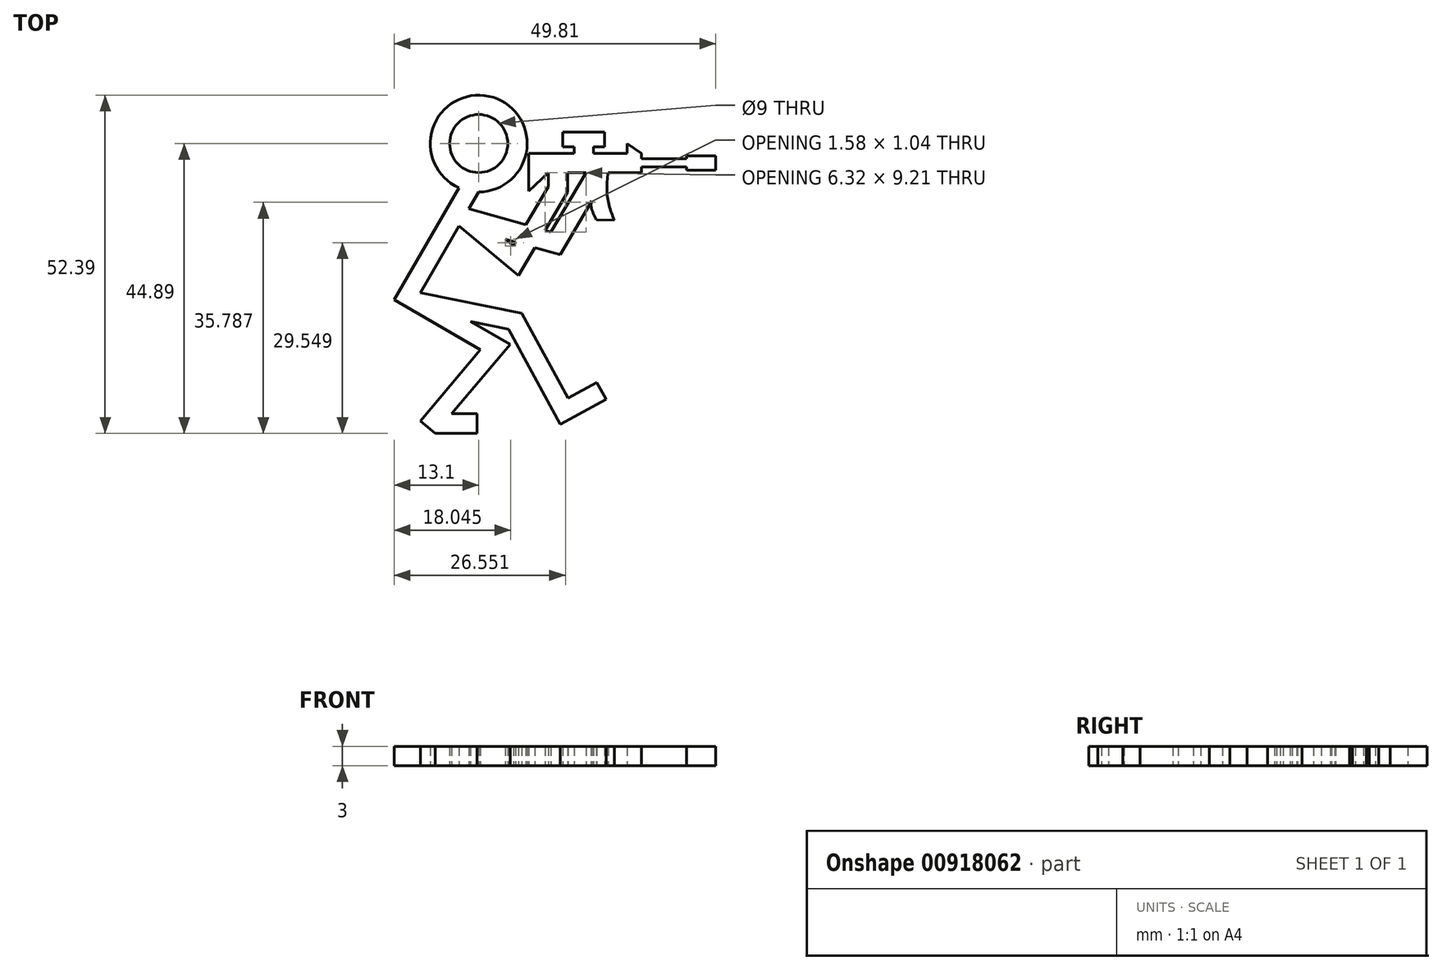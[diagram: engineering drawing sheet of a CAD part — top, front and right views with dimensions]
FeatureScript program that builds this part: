
annotation { "Feature Type Name" : "Feature", "Feature Type Description" : "" }
export const myFeature = defineFeature(function(context is Context, id is Id, definition is map)
    precondition{}
    {
        {
            var Q0;
            Q0=qCreatedBy(makeId("Top.planeOp"),FACE);
            var sketch = newSketch(context, id + "F0", { "sketchPlane" : qUnion([Q0])});
            skCircle(sketch, "E0", {"center": v(0, 0) * mm, "radius": 7.5 * mm});
            skCircle(sketch, "E1.0", {"center": v(0, 0) * mm, "radius": 4.5 * mm});
            skLineSegment(sketch, "E2", {"start": v(0, -7.5) * mm, "end": v(-10.5, -25.7) * mm});
            skLineSegment(sketch, "E3", {"start": v(-10.5, -25.7) * mm, "end": v(-13.1, -24.2) * mm});
            skLineSegment(sketch, "E4", {"start": v(-13.1, -24.2) * mm, "end": v(-3.08, -6.84) * mm});
            skLineSegment(sketch, "E5", {"start": v(0, -7.5) * mm, "end": v(0, -12.14) * mm, "construction": true});
            skLineSegment(sketch, "E6", {"start": v(-10.5, -25.7) * mm, "end": v(0.27, -31.9) * mm});
            skLineSegment(sketch, "E7", {"start": v(0.27, -31.9) * mm, "end": v(-9, -42.96) * mm});
            skLineSegment(sketch, "E8", {"start": v(-9, -42.96) * mm, "end": v(-6.7, -44.89) * mm});
            skLineSegment(sketch, "E9", {"start": v(-6.7, -44.89) * mm, "end": v(4.87, -31.1) * mm});
            skLineSegment(sketch, "E10", {"start": v(4.87, -31.1) * mm, "end": v(-9, -23.1) * mm});
            skLineSegment(sketch, "E11", {"start": v(-10.5, -25.7) * mm, "end": v(4.62, -28.75) * mm});
            skLineSegment(sketch, "E12", {"start": v(4.62, -28.75) * mm, "end": v(12.65, -43.5) * mm});
            skLineSegment(sketch, "E13", {"start": v(12.65, -43.5) * mm, "end": v(15.29, -42.07) * mm});
            skLineSegment(sketch, "E14", {"start": v(15.29, -42.07) * mm, "end": v(6.68, -26.26) * mm});
            skLineSegment(sketch, "E15", {"start": v(6.68, -26.26) * mm, "end": v(-9, -23.1) * mm});
            skLineSegment(sketch, "E16", {"start": v(-1.5, -10.1) * mm, "end": v(5.4, -15.86) * mm});
            skLineSegment(sketch, "E17", {"start": v(5.4, -15.86) * mm, "end": v(10.79, -6.68) * mm});
            skLineSegment(sketch, "E18", {"start": v(10.79, -6.68) * mm, "end": v(10.79, -4.5) * mm});
            skLineSegment(sketch, "E19", {"start": v(10.79, -4.5) * mm, "end": v(13.79, -4.5) * mm});
            skLineSegment(sketch, "E20", {"start": v(13.79, -4.5) * mm, "end": v(13.79, -7.5) * mm});
            skLineSegment(sketch, "E21", {"start": v(13.79, -7.5) * mm, "end": v(6.18, -20.43) * mm});
            skLineSegment(sketch, "E22", {"start": v(6.18, -20.43) * mm, "end": v(-3.02, -12.74) * mm});
            skLineSegment(sketch, "E23", {"start": v(4.15, -14.82) * mm, "end": v(12.61, -17.23) * mm});
            skLineSegment(sketch, "E24", {"start": v(12.61, -17.23) * mm, "end": v(20.1, -4.5) * mm});
            skLineSegment(sketch, "E25", {"start": v(20.1, -4.5) * mm, "end": v(16.61, -4.5) * mm});
            skLineSegment(sketch, "E26", {"start": v(16.61, -4.5) * mm, "end": v(11.2, -13.7) * mm});
            skLineSegment(sketch, "E27", {"start": v(11.2, -13.7) * mm, "end": v(-1.5, -10.1) * mm});
            skLineSegment(sketch, "E28.bottom", {"start": v(8.79, -4.5) * mm, "end": v(25.18, -4.5) * mm});
            skLineSegment(sketch, "E28.top", {"start": v(8.79, -1.5) * mm, "end": v(25.18, -1.5) * mm});
            skLineSegment(sketch, "E28.left", {"start": v(8.79, -4.5) * mm, "end": v(8.79, -1.5) * mm});
            skLineSegment(sketch, "E28.right", {"start": v(25.18, -4.5) * mm, "end": v(25.18, -1.5) * mm});
            skLineSegment(sketch, "E29.bottom", {"start": v(14.79, -1.5) * mm, "end": v(17.79, -1.5) * mm});
            skLineSegment(sketch, "E29.top", {"start": v(14.79, -0.5) * mm, "end": v(17.79, -0.5) * mm});
            skLineSegment(sketch, "E29.left", {"start": v(14.79, -1.5) * mm, "end": v(14.79, -0.5) * mm});
            skLineSegment(sketch, "E29.right", {"start": v(17.79, -1.5) * mm, "end": v(17.79, -0.5) * mm});
            skLineSegment(sketch, "E30", {"start": v(25.18, -1.5) * mm, "end": v(23, 0) * mm});
            skLineSegment(sketch, "E31", {"start": v(23, 0) * mm, "end": v(23, -1.5) * mm});
            skPoint(sketch, "E32.orphan", {"position": v(8.72, -16.12) * mm});
            skFitSpline(sketch, "E33", {"points": [v(20.1, -4.5) * mm, v(21.04, -11.87) * mm], "startDerivative": vector(-1.8, -7.95) * mm, "endDerivative": vector(2.97, -6.02) * mm});
            skFitSpline(sketch, "E34", {"points": [v(17.5, -8.9) * mm, v(18.24, -11.84) * mm], "startDerivative": vector(-0.96, -3.44) * mm, "endDerivative": vector(1.53, -3.3) * mm});
            skLineSegment(sketch, "E35", {"start": v(18.24, -11.84) * mm, "end": v(21.04, -11.87) * mm});
            skLineSegment(sketch, "E36.bottom", {"start": v(13, -0.5) * mm, "end": v(19.49, -0.5) * mm});
            skLineSegment(sketch, "E36.top", {"start": v(13, 1.78) * mm, "end": v(19.49, 1.78) * mm});
            skLineSegment(sketch, "E36.left", {"start": v(13, -0.5) * mm, "end": v(13, 1.78) * mm});
            skLineSegment(sketch, "E36.right", {"start": v(19.49, -0.5) * mm, "end": v(19.49, 1.78) * mm});
            skLineSegment(sketch, "E37", {"start": v(8.79, -1.5) * mm, "end": v(7.75, -1.5) * mm});
            skLineSegment(sketch, "E38", {"start": v(7.75, -1.5) * mm, "end": v(7.75, -7.34) * mm});
            skLineSegment(sketch, "E39", {"start": v(7.75, -7.34) * mm, "end": v(10.79, -4.5) * mm});
            skLineSegment(sketch, "E40.bottom", {"start": v(25.18, -2.36) * mm, "end": v(32.2, -2.36) * mm});
            skLineSegment(sketch, "E40.top", {"start": v(25.18, -3.64) * mm, "end": v(32.2, -3.64) * mm});
            skLineSegment(sketch, "E40.left", {"start": v(25.18, -2.36) * mm, "end": v(25.18, -3.64) * mm});
            skLineSegment(sketch, "E40.right", {"start": v(32.2, -2.36) * mm, "end": v(32.2, -3.64) * mm});
            skLineSegment(sketch, "E41.bottom", {"start": v(32.2, -1.92) * mm, "end": v(36.71, -1.92) * mm});
            skLineSegment(sketch, "E41.top", {"start": v(32.2, -4.1) * mm, "end": v(36.71, -4.1) * mm});
            skLineSegment(sketch, "E41.left", {"start": v(32.2, -1.92) * mm, "end": v(32.2, -4.1) * mm});
            skLineSegment(sketch, "E41.right", {"start": v(36.71, -1.92) * mm, "end": v(36.71, -4.1) * mm});
            skLineSegment(sketch, "E42", {"start": v(15.29, -42.07) * mm, "end": v(19.73, -39.65) * mm});
            skLineSegment(sketch, "E43", {"start": v(19.73, -39.65) * mm, "end": v(18.3, -37) * mm});
            skLineSegment(sketch, "E44", {"start": v(18.3, -37) * mm, "end": v(13.85, -39.42) * mm});
            skLineSegment(sketch, "E45", {"start": v(-6.7, -44.89) * mm, "end": v(-0.28, -44.89) * mm});
            skLineSegment(sketch, "E46", {"start": v(-0.28, -44.89) * mm, "end": v(-0.28, -41.86) * mm});
            skLineSegment(sketch, "E47", {"start": v(-0.28, -41.86) * mm, "end": v(-4.16, -41.86) * mm});
            skSolve(sketch);
        }
        {
            var Q0;
            {var subQ0=sQuery(id+"F0.wireOp",EDGE,"E28.left");var subQ1=makeQuery(id+"F0.imprint","IMPRINT",EDGE,{"derivedFrom":subQ0});var subQ2=sQuery(id+"F0.wireOp",EDGE,"E19");var subQ3=makeQuery(id+"F0.imprint","IMPRINT",EDGE,{"derivedFrom":subQ2});var subQ15=sQuery(id+"F0.wireOp",EDGE,"E18");var subQ17=sQuery(id+"F0.wireOp",EDGE,"E30");var subQ21=sQuery(id+"F0.wireOp",EDGE,"E25");var subQ22=makeQuery(id+"F0.imprint","IMPRINT",EDGE,{"derivedFrom":subQ21});var subQ23=sQuery(id+"F0.wireOp",EDGE,"E33");var subQ31=sQuery(id+"F0.wireOp",EDGE,"E40.bottom");var subQ41=sQuery(id+"F0.wireOp",EDGE,"E27");var subQ44=sQuery(id+"F0.wireOp",EDGE,"E17");var subQ45=makeQuery(id+"F0.imprint","INTERSECT",VERTEX,{"derivedFrom":[subQ44,subQ41]});var subQ47=makeQuery(id+"F0.imprint","IMPRINT",EDGE,{"disambiguationData":[TD([[subQ45,1.0]])],"derivedFrom":subQ44});var subQ56=sQuery(id+"F0.wireOp",EDGE,"E22");var subQ59=sQuery(id+"F0.wireOp",EDGE,"E11");var subQ60=sQuery(id+"F0.wireOp",EDGE,"E6");var subQ61=sQuery(id+"F0.wireOp",EDGE,"E3");var subQ64=sQuery(id+"F0.wireOp",EDGE,"E10");var subQ67=makeQuery(id+"F0.imprint","INTERSECT",VERTEX,{"derivedFrom":[subQ64,subQ59]});var subQ68=makeQuery(id+"F0.imprint","IMPRINT",EDGE,{"disambiguationData":[TD([[subQ67,-1.0]])],"derivedFrom":subQ64});var subQ75=sQuery(id+"F0.wireOp",EDGE,"E40.right");var subQ76=makeQuery(id+"F0.imprint","IMPRINT",EDGE,{"derivedFrom":subQ75});var subQ77=sQuery(id+"F0.wireOp",EDGE,"E29.top");var subQ78=makeQuery(id+"F0.imprint","IMPRINT",EDGE,{"derivedFrom":subQ77});var subQ79=sQuery(id+"F0.wireOp",EDGE,"E12");var subQ84=sQuery(id+"F0.wireOp",EDGE,"E42");var subQ91=sQuery(id+"F0.wireOp",EDGE,"E45");Q0=qUnion([makeQuery(id+"F0.imprint","IMPRINT",FACE,{"disambiguationData":[TD([[makeQuery(id+"F0.imprint","IMPRINT",EDGE,{"derivedFrom":subQ91}),1.0]])]}),makeQuery(id+"F0.imprint","IMPRINT",FACE,{"disambiguationData":[TD([[makeQuery(id+"F0.imprint","IMPRINT",EDGE,{"derivedFrom":subQ84}),1.0]])]}),makeQuery(id+"F0.imprint","IMPRINT",FACE,{"disambiguationData":[TD([[makeQuery(id+"F0.imprint","IMPRINT",EDGE,{"derivedFrom":subQ23}),-1.0]])]}),makeQuery(id+"F0.imprint","IMPRINT",FACE,{"disambiguationData":[TD([[subQ1,1.0]])]}),makeQuery(id+"F0.imprint","IMPRINT",FACE,{"disambiguationData":[TD([[makeQuery(id+"F0.imprint","IMPRINT",EDGE,{"derivedFrom":subQ17}),1.0]])]}),makeQuery(id+"F0.imprint","IMPRINT",FACE,{"disambiguationData":[TD([[subQ78,1.0]])]}),makeQuery(id+"F0.imprint","IMPRINT",FACE,{"disambiguationData":[TD([[subQ76,1.0]])]}),makeQuery(id+"F0.imprint","IMPRINT",FACE,{"disambiguationData":[TD([[makeQuery(id+"F0.imprint","IMPRINT",EDGE,{"derivedFrom":sQuery(id+"F0.wireOp",EDGE,"E1.0")}),-1.0]])]}),makeQuery(id+"F0.imprint","IMPRINT",FACE,{"disambiguationData":[TD([[makeQuery(id+"F0.imprint","IMPRINT",EDGE,{"derivedFrom":subQ60}),1.0]])]}),makeQuery(id+"F0.imprint","IMPRINT",FACE,{"disambiguationData":[TD([[makeQuery(id+"F0.imprint","IMPRINT",EDGE,{"derivedFrom":subQ79}),1.0]])]}),makeQuery(id+"F0.imprint","IMPRINT",FACE,{"disambiguationData":[TD([[subQ78,-1.0]])]}),makeQuery(id+"F0.imprint","IMPRINT",FACE,{"disambiguationData":[TD([[makeQuery(id+"F0.imprint","IMPRINT",EDGE,{"derivedFrom":subQ31}),-1.0]])]}),makeQuery(id+"F0.imprint","IMPRINT",FACE,{"disambiguationData":[TD([[makeQuery(id+"F0.imprint","IMPRINT",EDGE,{"derivedFrom":subQ61}),-1.0]])]}),makeQuery(id+"F0.imprint","IMPRINT",FACE,{"disambiguationData":[TD([[subQ68,1.0]])]}),makeQuery(id+"F0.imprint","IMPRINT",FACE,{"disambiguationData":[TD([[subQ47,1.0]])]}),makeQuery(id+"F0.imprint","IMPRINT",FACE,{"disambiguationData":[TD([[makeQuery(id+"F0.imprint","IMPRINT",EDGE,{"derivedFrom":subQ15}),-1.0]])]}),makeQuery(id+"F0.imprint","IMPRINT",FACE,{"disambiguationData":[TD([[makeQuery(id+"F0.imprint","IMPRINT",EDGE,{"derivedFrom":subQ56}),-1.0]])]}),makeQuery(id+"F0.imprint","IMPRINT",FACE,{"disambiguationData":[TD([[subQ47,-1.0]])]}),makeQuery(id+"F0.imprint","IMPRINT",FACE,{"disambiguationData":[TD([[subQ22,1.0]])]}),makeQuery(id+"F0.imprint","IMPRINT",FACE,{"disambiguationData":[TD([[subQ3,1.0]])]})]);}
            extrude(context, id + "F1", {"entities" : qUnion([Q0]), "depth" : 3 * mm, "offsetDistance" : 25 * mm});
        }
    });
